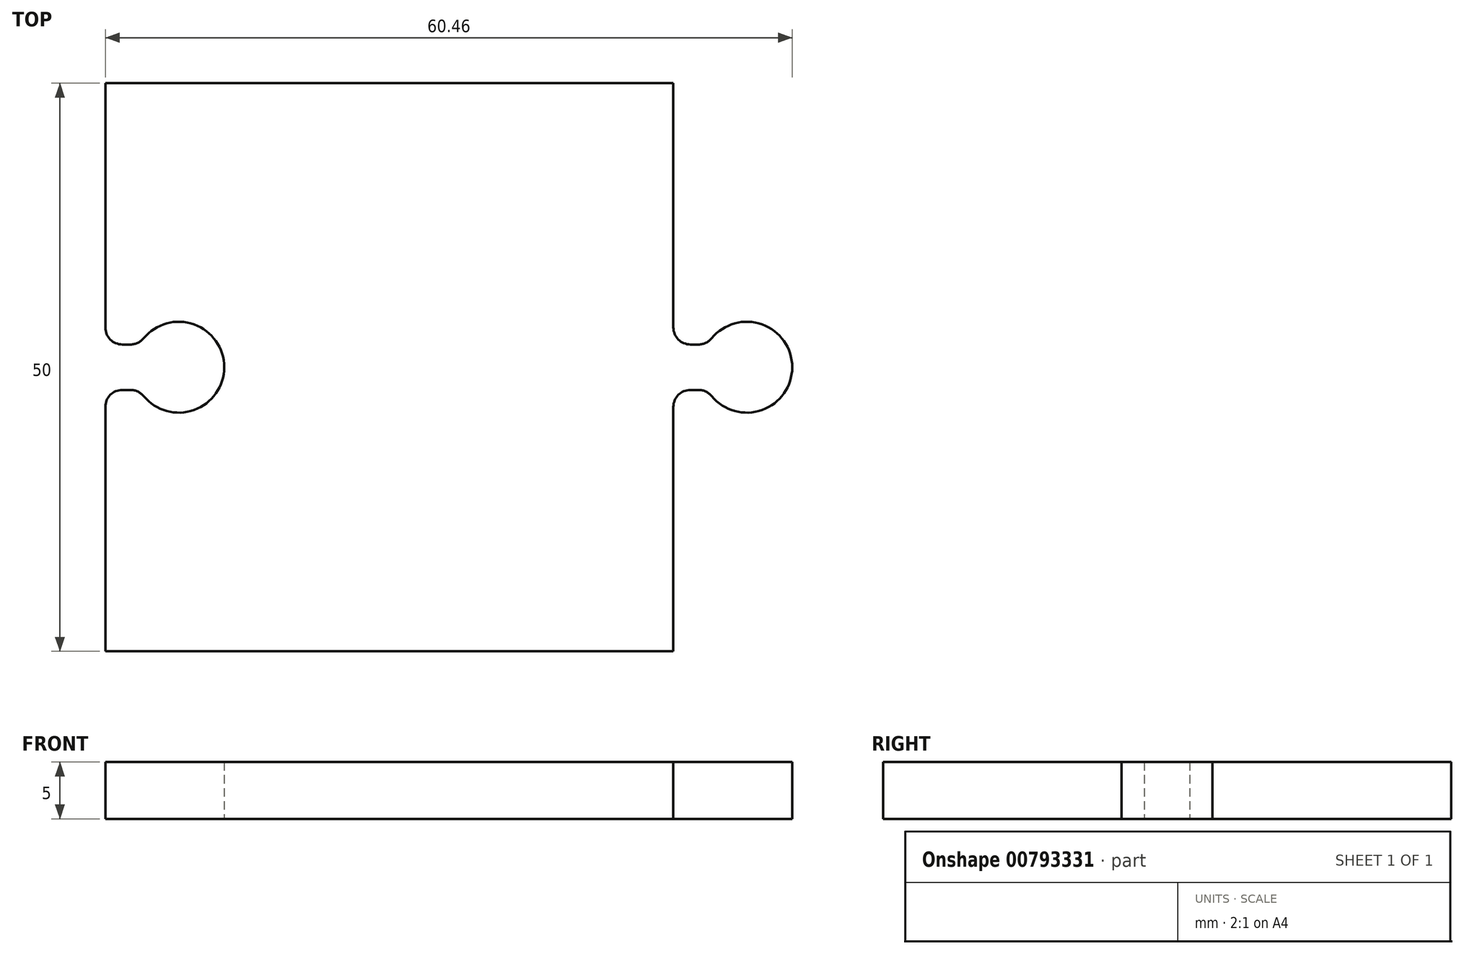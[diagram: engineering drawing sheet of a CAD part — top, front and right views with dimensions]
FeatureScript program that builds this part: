
annotation { "Feature Type Name" : "Feature", "Feature Type Description" : "" }
export const myFeature = defineFeature(function(context is Context, id is Id, definition is map)
    precondition{}
    {
        {
            var Q0;
            Q0=qCreatedBy(makeId("Top.planeOp"),FACE);
            var sketch = newSketch(context, id + "F0", { "sketchPlane" : qUnion([Q0])});
            skLineSegment(sketch, "E0.bottom", {"start": v(-15.19, 21.72) * mm, "end": v(34.81, 21.72) * mm});
            skLineSegment(sketch, "E0.top", {"start": v(-15.19, -28.28) * mm, "end": v(34.81, -28.28) * mm});
            skLineSegment(sketch, "E0.left", {"start": v(-15.19, 21.72) * mm, "end": v(-15.19, 0.22) * mm});
            skLineSegment(sketch, "E0.right", {"start": v(34.81, 21.72) * mm, "end": v(34.81, 0.22) * mm});
            skLineSegment(sketch, "E1", {"start": v(34.81, -3.28) * mm, "end": v(34.81, -1.28) * mm});
            skLineSegment(sketch, "E2", {"start": v(34.81, -3.28) * mm, "end": v(34.81, -5.28) * mm});
            skArc(sketch, "E3", {"start": v(38.18, -5.83) * mm, "mid": v(45.27, -3.28) * mm, "end": v(38.18, -0.73) * mm});
            skLineSegment(sketch, "E4", {"start": v(36.31, -1.28) * mm, "end": v(37.03, -1.28) * mm});
            skLineSegment(sketch, "E5", {"start": v(36.31, -5.28) * mm, "end": v(37.03, -5.28) * mm});
            skPoint(sketch, "E6.newPointA", {"position": v(34.81, -28.28) * mm});
            skArc(sketch, "E6.filletArc", {"start": v(34.81, 0.22) * mm, "mid": v(35.25, -0.84) * mm, "end": v(36.31, -1.28) * mm});
            skLineSegment(sketch, "E7", {"start": v(34.81, -6.78) * mm, "end": v(34.81, -28.28) * mm});
            skPoint(sketch, "E8.visualSharp", {"position": v(34.81, -5.28) * mm});
            skArc(sketch, "E8.filletArc", {"start": v(36.31, -5.28) * mm, "mid": v(35.25, -5.72) * mm, "end": v(34.81, -6.78) * mm});
            skPoint(sketch, "E9.visualSharp", {"position": v(37.8, -5.28) * mm});
            skArc(sketch, "E9.filletArc", {"start": v(38.18, -5.83) * mm, "mid": v(37.67, -5.42) * mm, "end": v(37.03, -5.28) * mm});
            skPoint(sketch, "E10.visualSharp", {"position": v(37.8, -1.28) * mm});
            skArc(sketch, "E10.filletArc", {"start": v(37.03, -1.28) * mm, "mid": v(37.67, -1.14) * mm, "end": v(38.18, -0.73) * mm});
            skArc(sketch, "E11", {"start": v(-11.82, -5.83) * mm, "mid": v(-4.73, -3.28) * mm, "end": v(-11.82, -0.73) * mm});
            skLineSegment(sketch, "E12", {"start": v(-13.69, -1.28) * mm, "end": v(-12.97, -1.28) * mm});
            skLineSegment(sketch, "E13", {"start": v(-13.69, -5.28) * mm, "end": v(-12.97, -5.28) * mm});
            skLineSegment(sketch, "E14.trimOffspring", {"start": v(-15.19, -6.78) * mm, "end": v(-15.19, -28.28) * mm});
            skPoint(sketch, "E15.orphan", {"position": v(-15.19, -3.28) * mm});
            skPoint(sketch, "E16.visualSharp", {"position": v(-15.19, -1.28) * mm});
            skArc(sketch, "E16.filletArc", {"start": v(-15.19, 0.22) * mm, "mid": v(-14.75, -0.84) * mm, "end": v(-13.69, -1.28) * mm});
            skPoint(sketch, "E17.visualSharp", {"position": v(-12.2, -1.28) * mm});
            skArc(sketch, "E17.filletArc", {"start": v(-12.97, -1.28) * mm, "mid": v(-12.33, -1.14) * mm, "end": v(-11.82, -0.73) * mm});
            skPoint(sketch, "E18.visualSharp", {"position": v(-12.2, -5.28) * mm});
            skArc(sketch, "E18.filletArc", {"start": v(-11.82, -5.83) * mm, "mid": v(-12.33, -5.42) * mm, "end": v(-12.97, -5.28) * mm});
            skPoint(sketch, "E19.visualSharp", {"position": v(-15.19, -5.28) * mm});
            skArc(sketch, "E19.filletArc", {"start": v(-13.69, -5.28) * mm, "mid": v(-14.75, -5.72) * mm, "end": v(-15.19, -6.78) * mm});
            skSolve(sketch);
        }
        {
            var Q0;
            Q0 = qSketchRegion(id + "F0", true);
            extrude(context, id + "F1", {"entities" : qUnion([Q0]), "depth" : 5 * mm, "offsetDistance" : 25 * mm});
        }
    });
